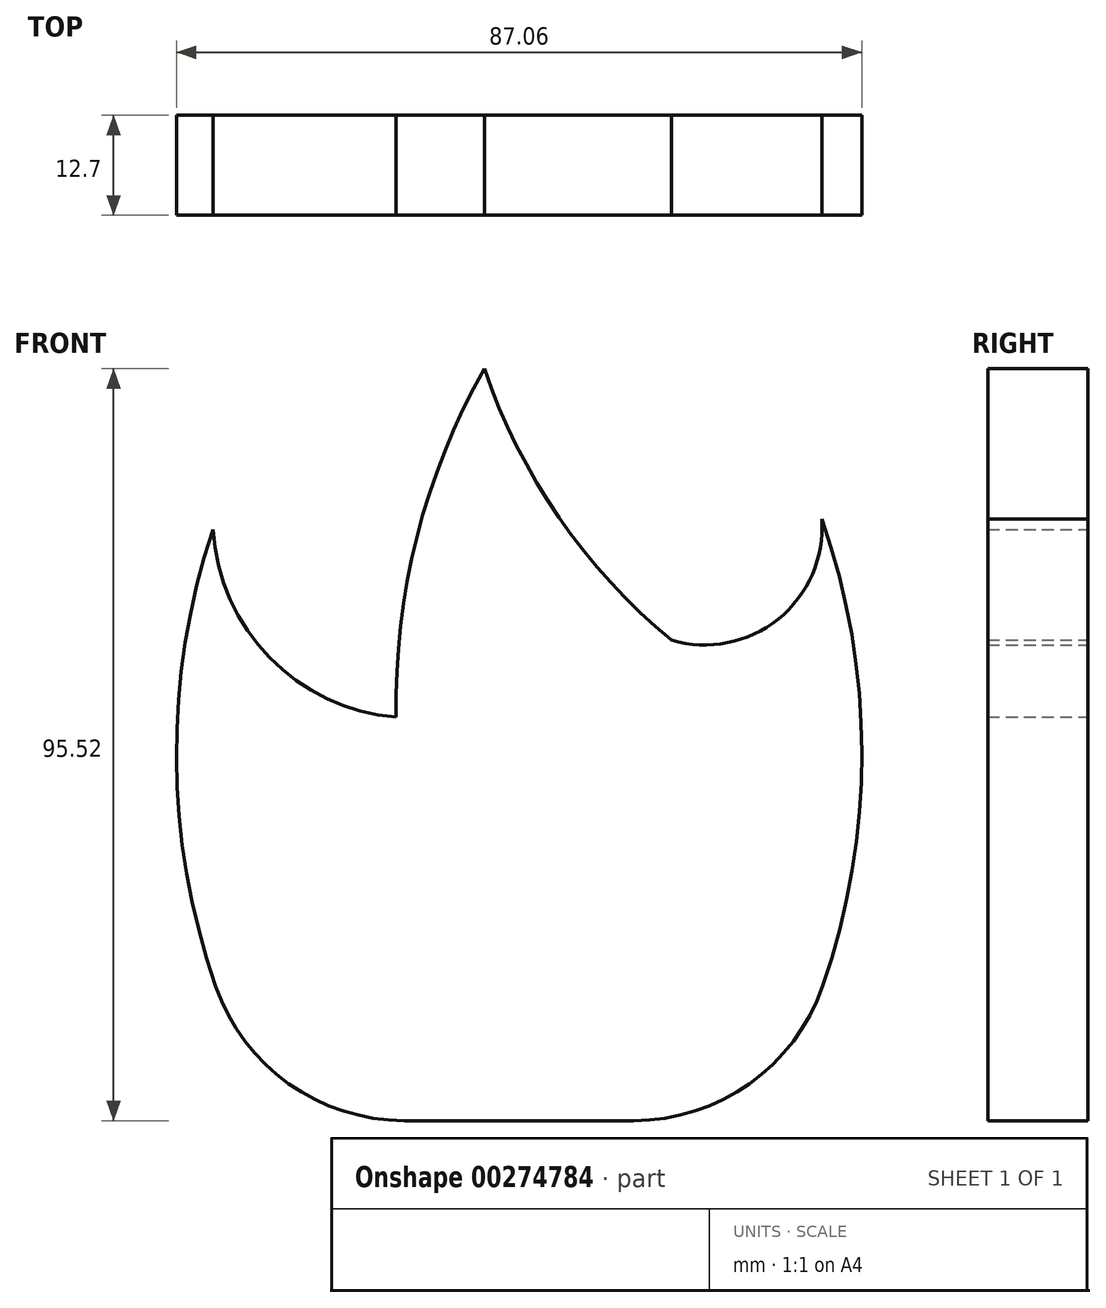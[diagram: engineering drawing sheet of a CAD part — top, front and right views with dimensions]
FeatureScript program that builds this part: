
annotation { "Feature Type Name" : "Feature", "Feature Type Description" : "" }
export const myFeature = defineFeature(function(context is Context, id is Id, definition is map)
    precondition{}
    {
        {
            var Q0;
            Q0=qCreatedBy(makeId("Front.planeOp"),FACE);
            var sketch = newSketch(context, id + "F0", { "sketchPlane" : qUnion([Q0])});
            skArc(sketch, "E0", {"start": v(-57.27, 72.69) * mm, "mid": v(-62.46, 32.93) * mm, "end": v(-49.85, -5.13) * mm});
            skLineSegment(sketch, "E1", {"start": v(-49.85, -5.13) * mm, "end": v(11.18, -5.13) * mm});
            skArc(sketch, "E2.MirrorCS", {"start": v(19.1, 71.29) * mm, "mid": v(23.72, 32.2) * mm, "end": v(11.18, -5.13) * mm});
            skPoint(sketch, "E3.start.orphan", {"position": v(-19.34, -5.13) * mm});
            skArc(sketch, "E4", {"start": v(-58.24, 72.69) * mm, "mid": v(-51.95, 54.71) * mm, "end": v(-34.95, 46.13) * mm});
            skArc(sketch, "E5", {"start": v(-23.76, 90.4) * mm, "mid": v(-32.33, 69.01) * mm, "end": v(-34.95, 46.13) * mm});
            skArc(sketch, "E6", {"start": v(-23.76, 90.4) * mm, "mid": v(-14.27, 71.5) * mm, "end": v(0, 55.91) * mm});
            skArc(sketch, "E7", {"start": v(0, 55.91) * mm, "mid": v(13.58, 58.6) * mm, "end": v(19.1, 71.29) * mm});
            skSolve(sketch);
        }
        {
            var Q0;
            Q0 = qSketchRegion(id + "F0", true);
            extrude(context, id + "F1", {"entities" : qUnion([Q0]), "depth" : 12.7 * mm});
        }
        {
            var Q0;
            Q0=makeQuery(id+"F1.opExtrude","SWEPT_EDGE",EDGE,{"disambiguationData":[OSD([sQuery(id+"F0.wireOp",EDGE,"E0"),sQuery(id+"F0.wireOp",EDGE,"E1")])]});
            fillet(context, id + "F2", {"entities" : qUnion([Q0]), "radius" : 25.4 * mm, "tangentPropagation" : true, "allowEdgeOverflow" : false});
        }
        {
            var Q0;
            Q0=makeQuery(id+"F1.opExtrude","SWEPT_EDGE",EDGE,{"disambiguationData":[OSD([sQuery(id+"F0.wireOp",EDGE,"E1"),sQuery(id+"F0.wireOp",EDGE,"E2.MirrorCS")])]});
            fillet(context, id + "F3", {"entities" : qUnion([Q0]), "radius" : 25.4 * mm, "tangentPropagation" : true, "allowEdgeOverflow" : false});
        }
    });
